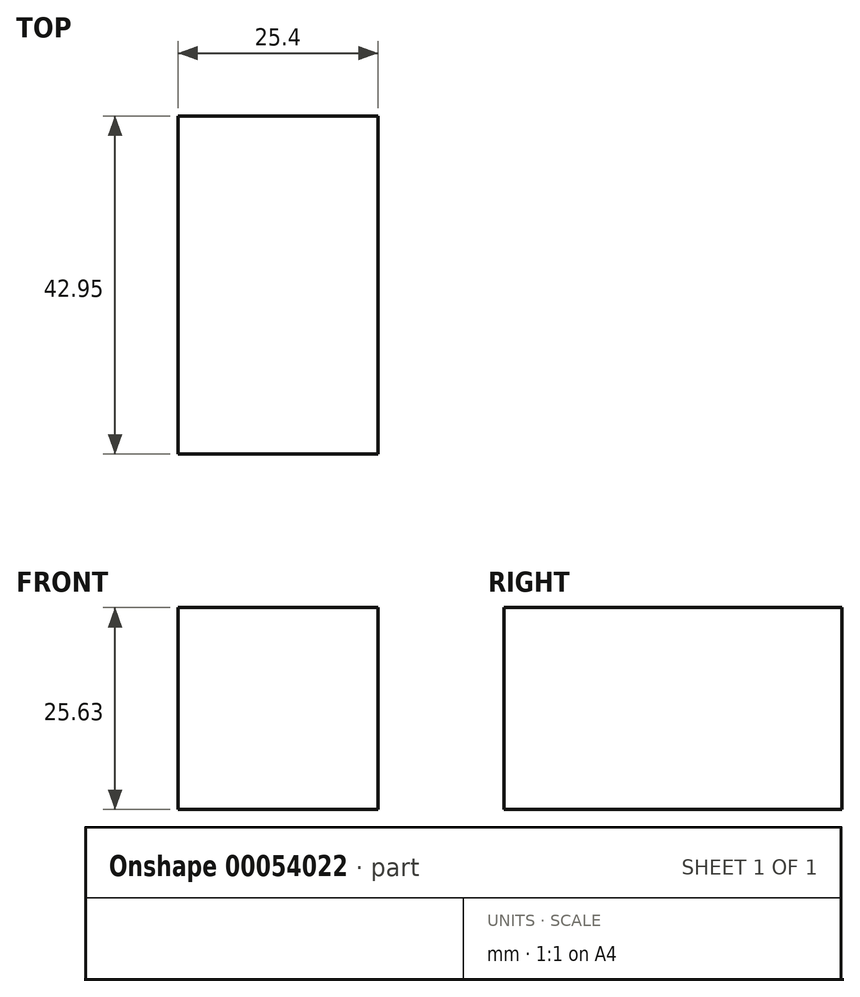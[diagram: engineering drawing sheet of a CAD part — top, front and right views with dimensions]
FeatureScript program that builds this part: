
annotation { "Feature Type Name" : "Feature", "Feature Type Description" : "" }
export const myFeature = defineFeature(function(context is Context, id is Id, definition is map)
    precondition{}
    {
        {
            var Q0;
            Q0=qCreatedBy(makeId("Right.planeOp"),FACE);
            var sketch = newSketch(context, id + "F0", { "sketchPlane" : qUnion([Q0])});
            skLineSegment(sketch, "E0.bottom", {"start": v(42.95, 33.83) * mm, "end": v(0, 33.83) * mm});
            skLineSegment(sketch, "E0.top", {"start": v(42.95, 8.2) * mm, "end": v(0, 8.2) * mm});
            skLineSegment(sketch, "E0.left", {"start": v(42.95, 33.83) * mm, "end": v(42.95, 8.2) * mm});
            skLineSegment(sketch, "E0.right", {"start": v(0, 33.83) * mm, "end": v(0, 8.2) * mm});
            skSolve(sketch);
        }
        {
            var Q0;
            Q0=makeQuery(id+"F0.imprint","IMPRINT",FACE,{"disambiguationData":[TD([[makeQuery(id+"F0.imprint","IMPRINT",EDGE,{"derivedFrom":sQuery(id+"F0.wireOp",EDGE,"E0.bottom")}),1.0]])]});
            extrude(context, id + "F1", {"entities" : qUnion([Q0]), "depth" : 25.4 * mm});
        }
    });
